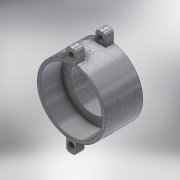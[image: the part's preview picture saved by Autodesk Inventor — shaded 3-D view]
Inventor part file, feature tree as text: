
AUTODESK INVENTOR PART (.ipt)
format: ipt  version: 2018 (Build 220112000, 112)  size: 211,456 bytes
history: native  units: in
note: dims shown in document units (in); Inventor stores cm internally (conversion verified against a paired STEP export)
features: move_body x2, direct_edit x1, fillet x1
ambient origin geometry x8: Origin, YZ Plane, XZ Plane, XY Plane, X Axis, Y Axis, Z Axis, Center Point
bodies: Solid1 (feature_tree)
feature tree (4):
  direct_edit  "Direct Edit4"
  fillet  "Fillet2"  Radius=0.7874in
  move_body  "Move8"
  move_body  "Move9"
